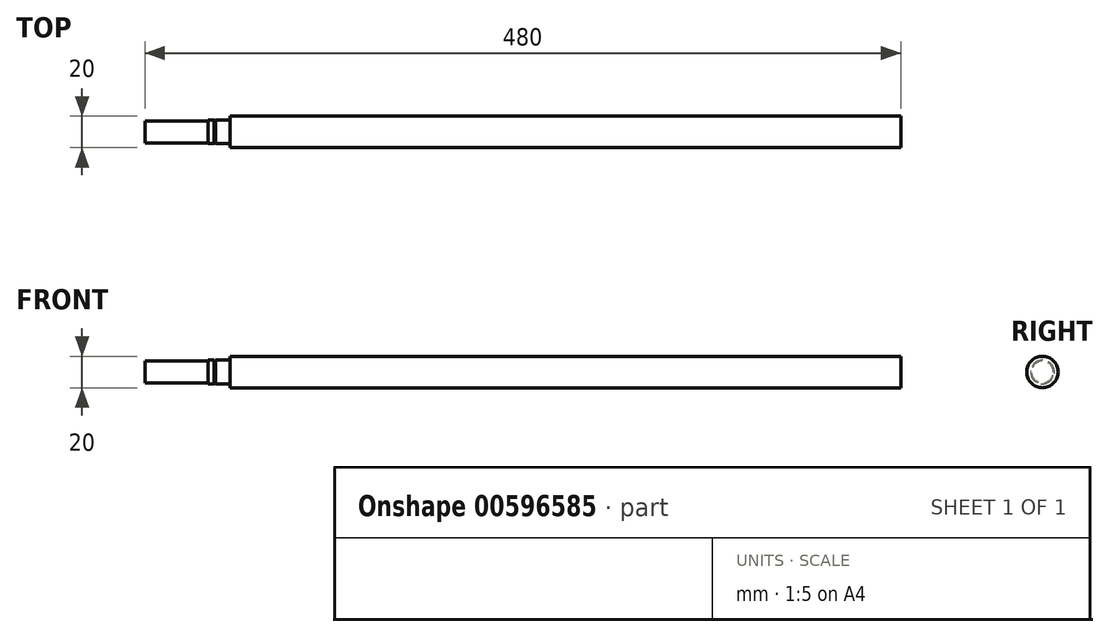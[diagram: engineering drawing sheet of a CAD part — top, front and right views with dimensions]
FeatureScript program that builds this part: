
annotation { "Feature Type Name" : "Feature", "Feature Type Description" : "" }
export const myFeature = defineFeature(function(context is Context, id is Id, definition is map)
    precondition{}
    {
        {
            var Q0;
            Q0=qCreatedBy(makeId("Front.planeOp"),FACE);
            var sketch = newSketch(context, id + "F0", { "sketchPlane" : qUnion([Q0])});
            skLineSegment(sketch, "E0", {"start": v(0, 0) * mm, "end": v(480, 0) * mm});
            skLineSegment(sketch, "E1", {"start": v(480, 0) * mm, "end": v(480, 10) * mm});
            skLineSegment(sketch, "E2", {"start": v(0, 0) * mm, "end": v(0, 7) * mm});
            skLineSegment(sketch, "E3", {"start": v(0, 7) * mm, "end": v(40, 7) * mm});
            skLineSegment(sketch, "E4", {"start": v(40, 7) * mm, "end": v(40, 7.5) * mm});
            skLineSegment(sketch, "E5", {"start": v(40, 7.5) * mm, "end": v(43.9, 7.5) * mm});
            skLineSegment(sketch, "E6", {"start": v(45, 7.5) * mm, "end": v(54, 7.5) * mm});
            skLineSegment(sketch, "E7", {"start": v(54, 7.5) * mm, "end": v(54, 10) * mm});
            skLineSegment(sketch, "E8", {"start": v(54, 10) * mm, "end": v(480, 10) * mm});
            skLineSegment(sketch, "E9", {"start": v(45, 7.5) * mm, "end": v(45, 7.15) * mm});
            skLineSegment(sketch, "E10", {"start": v(45, 7.15) * mm, "end": v(43.9, 7.15) * mm});
            skLineSegment(sketch, "E11", {"start": v(43.9, 7.15) * mm, "end": v(43.9, 7.5) * mm});
            skSolve(sketch);
        }
        {
            var Q0;
            Q0=makeQuery(id+"F0.imprint","IMPRINT",FACE,{"disambiguationData":[TD([[makeQuery(id+"F0.imprint","IMPRINT",EDGE,{"derivedFrom":sQuery(id+"F0.wireOp",EDGE,"E0")}),1.0]])]});
            var Q1;
            Q1=sQuery(id+"F0.wireOp",EDGE,"E0");
            revolve(context, id + "F1", {"entities" : qUnion([Q0]), "axis" : qUnion([Q1]), "revolveType" : RevolveType.FULL});
        }
    });
